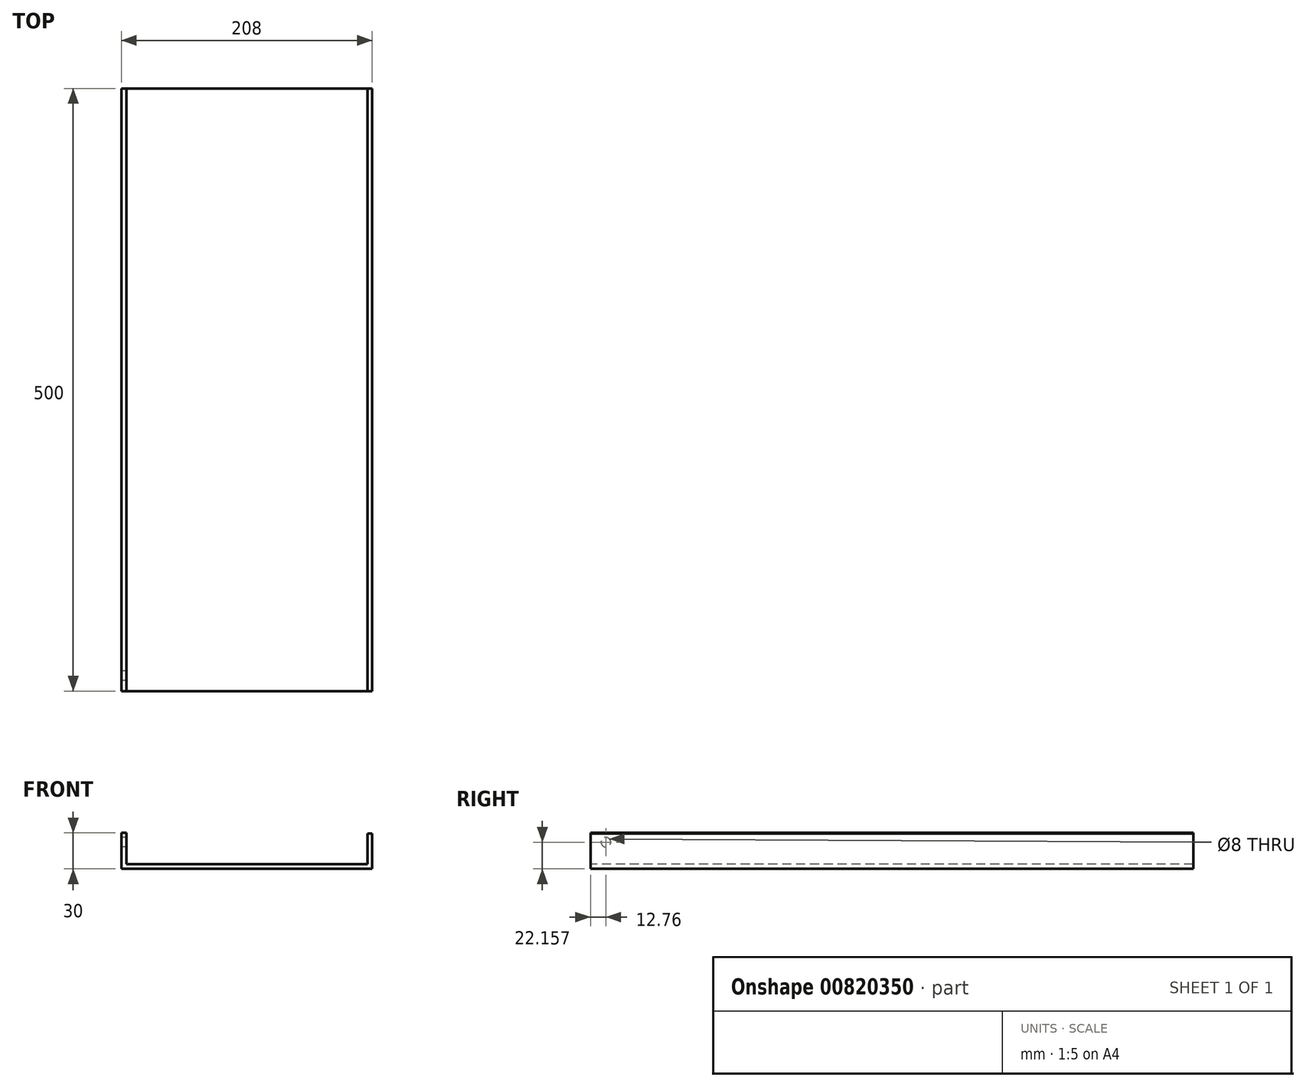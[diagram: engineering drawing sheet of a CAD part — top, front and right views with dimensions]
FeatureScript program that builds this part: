
annotation { "Feature Type Name" : "Feature", "Feature Type Description" : "" }
export const myFeature = defineFeature(function(context is Context, id is Id, definition is map)
    precondition{}
    {
        {
            var Q0;
            Q0=qCreatedBy(makeId("Front.planeOp"),FACE);
            var sketch = newSketch(context, id + "F0", { "sketchPlane" : qUnion([Q0])});
            skLineSegment(sketch, "E0.top", {"start": v(-104, 0) * mm, "end": v(104, 0) * mm});
            skLineSegment(sketch, "E0.left", {"start": v(-104, 30) * mm, "end": v(-104, 0) * mm});
            skLineSegment(sketch, "E0.right", {"start": v(104, 29.33) * mm, "end": v(104, 0) * mm});
            skLineSegment(sketch, "E1.top", {"start": v(-100, 4) * mm, "end": v(100, 4) * mm});
            skLineSegment(sketch, "E1.left", {"start": v(-100, 30) * mm, "end": v(-100, 4) * mm});
            skLineSegment(sketch, "E1.right", {"start": v(100, 29.33) * mm, "end": v(100, 4) * mm});
            skLineSegment(sketch, "E2", {"start": v(-104, 30) * mm, "end": v(-100, 30) * mm});
            skLineSegment(sketch, "E3", {"start": v(100, 29.33) * mm, "end": v(104, 29.33) * mm});
            skSolve(sketch);
        }
        {
            var Q0;
            Q0=makeQuery(id+"F0.imprint","IMPRINT",FACE,{"disambiguationData":[TD([[makeQuery(id+"F0.imprint","IMPRINT",EDGE,{"derivedFrom":sQuery(id+"F0.wireOp",EDGE,"E0.top")}),1.0]])]});
            extrude(context, id + "F1", {"entities" : qUnion([Q0]), "oppositeDirection" : true, "depth" : 500 * mm, "offsetDistance" : 25 * mm});
        }
        {
            var Q0;
            Q0=makeQuery(id+"F1.opExtrude","SWEPT_FACE",FACE,{"disambiguationData":[OSD([sQuery(id+"F0.wireOp",EDGE,"E0.left")])]});
            var sketch = newSketch(context, id + "F2", { "sketchPlane" : qUnion([Q0])});
            skCircle(sketch, "E4", {"center": v(-12.76, 22.16) * mm, "radius": 4 * mm});
            skSolve(sketch);
        }
        {
            var Q0;
            Q0=sQuery(id+"F2.wireOp",VERTEX,"E4.center");
            var Q1;
            Q1=makeQuery(id+"F1.opExtrude","SWEPT_BODY",BODY,{"disambiguationData":[OSD([sQuery(id+"F0.wireOp",EDGE,"E0.top"),sQuery(id+"F0.wireOp",EDGE,"E0.left"),sQuery(id+"F0.wireOp",EDGE,"E0.right"),sQuery(id+"F0.wireOp",EDGE,"E1.top"),sQuery(id+"F0.wireOp",EDGE,"E1.left"),sQuery(id+"F0.wireOp",EDGE,"E1.right"),sQuery(id+"F0.wireOp",EDGE,"E2"),sQuery(id+"F0.wireOp",EDGE,"E3")])]});
            hole(context, id + "F3", {"style" : HoleStyle.SIMPLE, "endStyle" : HoleEndStyle.BLIND, "holeDiameter" : 8 * mm, "majorDiameter" : 5 * mm, "holeDepth" : 12 * mm, "isTappedThrough" : true, "tappedDepth" : 12 * mm, "tapClearance" : 3, "locations" : qUnion([Q0]), "scope" : qUnion([Q1])});
        }
    });
